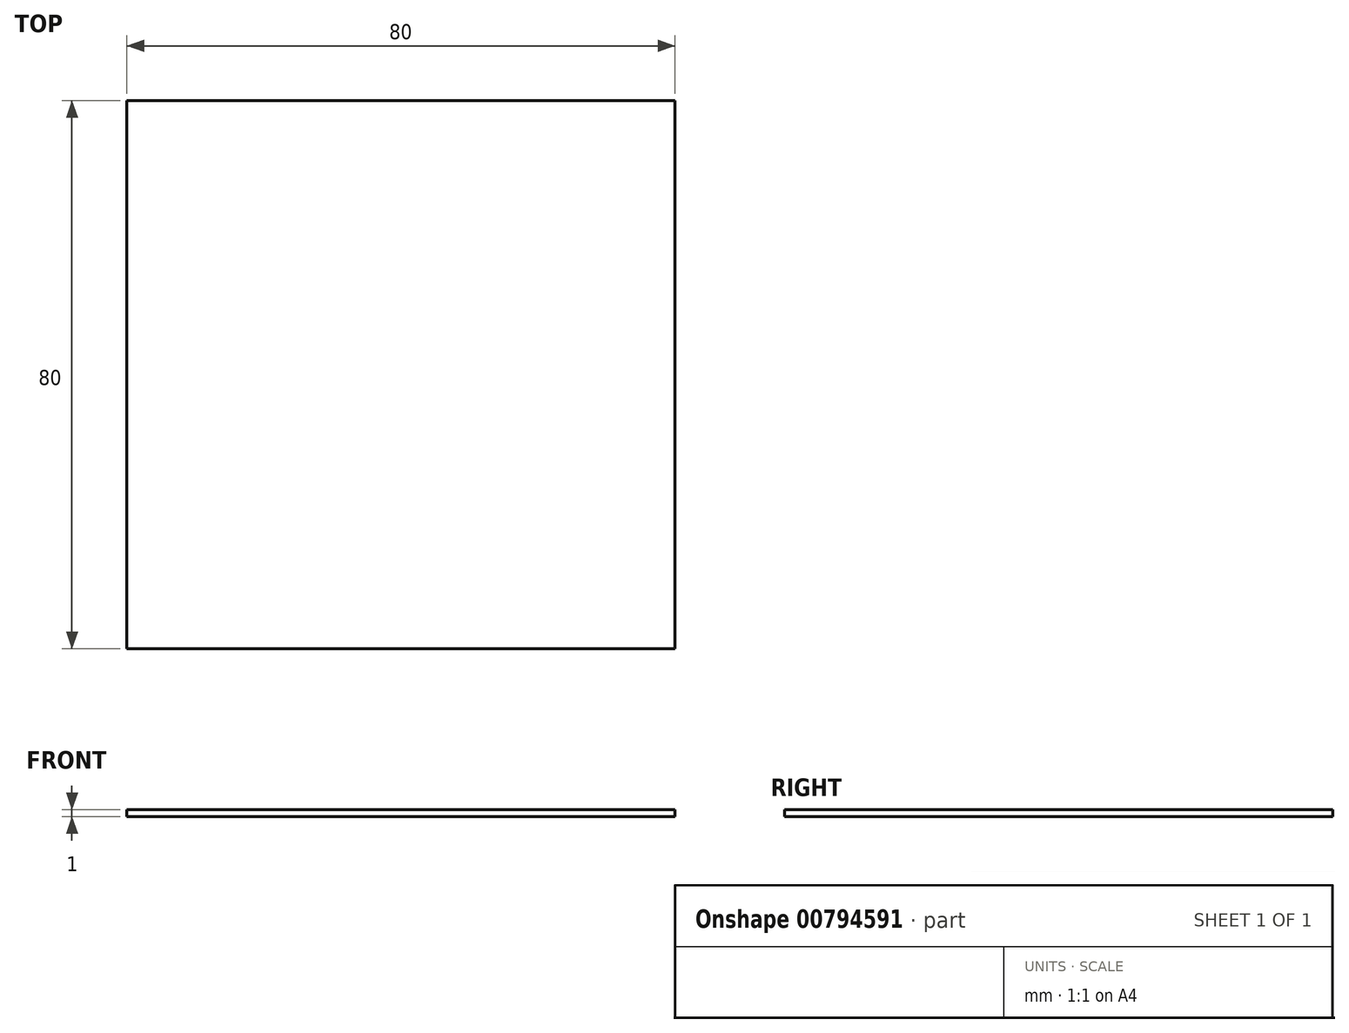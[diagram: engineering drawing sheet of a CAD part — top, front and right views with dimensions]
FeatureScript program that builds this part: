
annotation { "Feature Type Name" : "Feature", "Feature Type Description" : "" }
export const myFeature = defineFeature(function(context is Context, id is Id, definition is map)
    precondition{}
    {
        {
            var Q0;
            Q0=qCreatedBy(makeId("Top.planeOp"),FACE);
            var sketch = newSketch(context, id + "F0", { "sketchPlane" : qUnion([Q0])});
            skLineSegment(sketch, "E0.bottom", {"start": v(40, -40) * mm, "end": v(-40, -40) * mm});
            skLineSegment(sketch, "E0.top", {"start": v(40, 40) * mm, "end": v(-40, 40) * mm});
            skLineSegment(sketch, "E0.left", {"start": v(40, -40) * mm, "end": v(40, 40) * mm});
            skLineSegment(sketch, "E0.right", {"start": v(-40, -40) * mm, "end": v(-40, 40) * mm});
            skPoint(sketch, "E0.middle", {"position": v(0, 0) * mm});
            skSolve(sketch);
        }
        {
            var Q0;
            Q0=makeQuery(id+"F0.imprint","IMPRINT",FACE,{"disambiguationData":[TD([[makeQuery(id+"F0.imprint","IMPRINT",EDGE,{"derivedFrom":sQuery(id+"F0.wireOp",EDGE,"E0.bottom")}),-1.0]])]});
            extrude(context, id + "F1", {"entities" : qUnion([Q0]), "depth" : 1 * mm, "offsetDistance" : 25 * mm});
        }
    });
